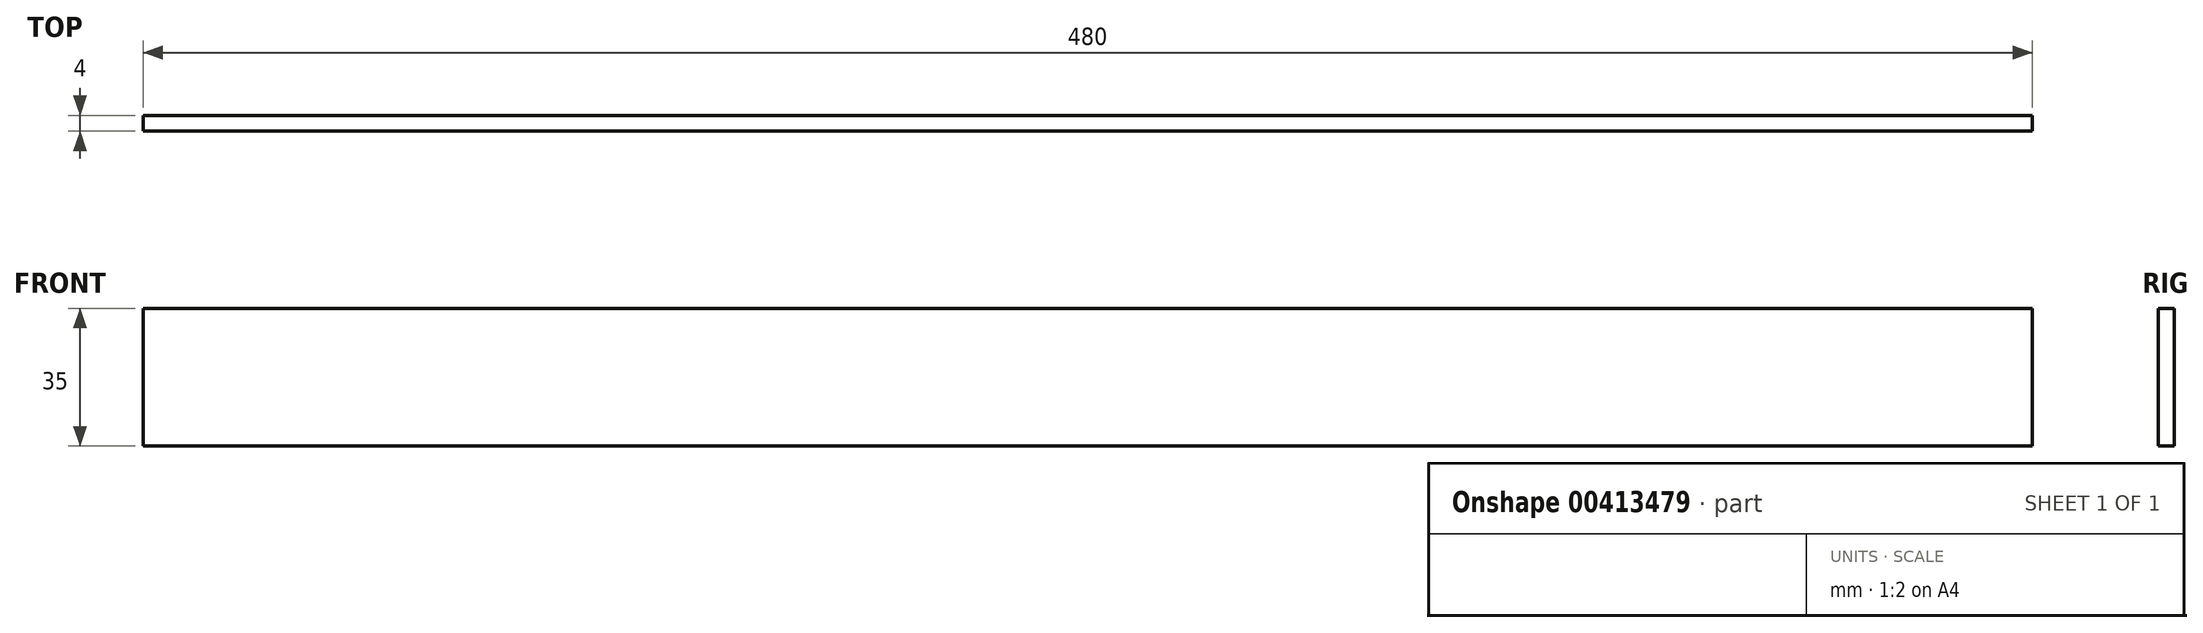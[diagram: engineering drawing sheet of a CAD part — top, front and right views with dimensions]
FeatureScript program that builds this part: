
annotation { "Feature Type Name" : "Feature", "Feature Type Description" : "" }
export const myFeature = defineFeature(function(context is Context, id is Id, definition is map)
    precondition{}
    {
        {
            var Q0;
            Q0=qCreatedBy(makeId("Front.planeOp"),FACE);
            var sketch = newSketch(context, id + "F0", { "sketchPlane" : qUnion([Q0])});
            skLineSegment(sketch, "E0.bottom", {"start": v(-240, 0) * mm, "end": v(240, 0) * mm});
            skLineSegment(sketch, "E0.top", {"start": v(-240, -35) * mm, "end": v(240, -35) * mm});
            skLineSegment(sketch, "E0.left", {"start": v(-240, 0) * mm, "end": v(-240, -35) * mm});
            skLineSegment(sketch, "E0.right", {"start": v(240, 0) * mm, "end": v(240, -35) * mm});
            skSolve(sketch);
        }
        {
            var Q0;
            Q0 = qSketchRegion(id + "F0", true);
            extrude(context, id + "F1", {"entities" : qUnion([Q0]), "depth" : 4 * mm});
        }
    });
